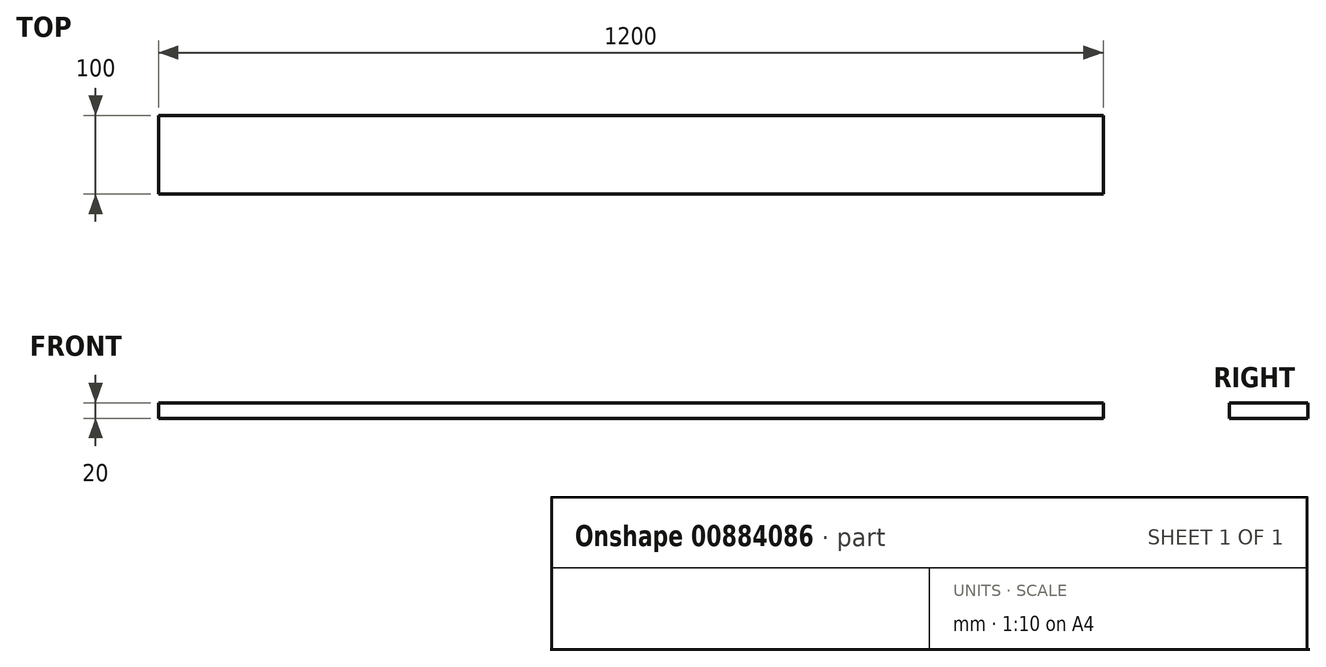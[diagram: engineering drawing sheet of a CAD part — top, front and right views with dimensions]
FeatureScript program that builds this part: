
annotation { "Feature Type Name" : "Feature", "Feature Type Description" : "" }
export const myFeature = defineFeature(function(context is Context, id is Id, definition is map)
    precondition{}
    {
        {
            var Q0;
            Q0=qCreatedBy(makeId("Top.planeOp"),FACE);
            var sketch = newSketch(context, id + "F0", { "sketchPlane" : qUnion([Q0])});
            skLineSegment(sketch, "E0.bottom", {"start": v(0, 0) * mm, "end": v(1200, 0) * mm});
            skLineSegment(sketch, "E0.top", {"start": v(0, 100) * mm, "end": v(1200, 100) * mm});
            skLineSegment(sketch, "E0.left", {"start": v(0, 0) * mm, "end": v(0, 100) * mm});
            skLineSegment(sketch, "E0.right", {"start": v(1200, 0) * mm, "end": v(1200, 100) * mm});
            skSolve(sketch);
        }
        {
            var Q0;
            Q0=makeQuery(id+"F0.imprint","IMPRINT",FACE,{"disambiguationData":[TD([[makeQuery(id+"F0.imprint","IMPRINT",EDGE,{"derivedFrom":sQuery(id+"F0.wireOp",EDGE,"E0.bottom")}),1.0]])]});
            extrude(context, id + "F1", {"entities" : qUnion([Q0]), "depth" : 20 * mm, "offsetDistance" : 25 * mm});
        }
    });
